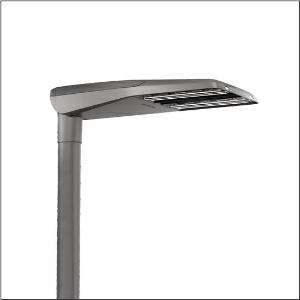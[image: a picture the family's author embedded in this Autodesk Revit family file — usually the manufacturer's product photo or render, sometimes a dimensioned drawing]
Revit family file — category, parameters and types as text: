
# Revit family: streetlight_sl_11_iq_midi___st1_2a_5xc3a51e08le_ac55
name_source: partatom
category: Lighting Fixtures
units: mm (PartAtom-declared; Revit-internal decimal feet)

## family parameters
Cut with Voids When Loaded = No
Host = Face
Light Source = No
Part Type = Normal
Room Calculation Point = No
Round Connector Dimension = Use Diameter
Shared = No

## types (1)
- --- (1 x LED, 9210 lm, 60.4 W, 3000K)
    Apparent Load = 60 VA
    CIE Flux Codes = 32 70 96 100 100
    Color Rendering = 70
    Color Temperature = 3000K
    Default Elevation = 1800 mm
    Description = Streetlight SL 11 iQ midi, mast luminaire, primary light control with 3 zone facetted reflector, of plastic, silver coated, highly specular, primary optical cover: cover, of PMMA, transparent, light distribution: ST1.2a, light emission: direct distribution, primary light characteristic: asymmetric, installation type: post-top, side-entry, LED, High Power LED, rated luminous flux: 9.210lm, luminous efficacy: 153lm/W, light colour: 730, colour temperature: 3000K, control: optimised constant luminous flux control (CLO 2.0), Desk-Remote (wireless, voltage-free reading and setting of iQ features in the workshop via application-optimized NFC function/RFID function), Light-Fading, Smart-Wire, Night-Set, Lumen-Switch, Temp-Guard, Auto-Match, with cable H07RN-F 5x 1.5mm², mains connection: 230..240V, AC, 50/60Hz, connection cable pre-assembled, cable length: 8,5m, start of lifetime: 60W, end of service life: 63W, reduction: 30W, luminaire housing, of diecast aluminium, powder-coated, Siteco® metallic grey (DB 702S), please order mast flange separately, inclination adjustable without tools: 0°, 5°, 10°, 15° (post-top) | 0°, -5°, -10°, -15° (side-entry), sealing non-destructively replaceable, multi-level sealing system, length: 780mm, width: 376mm, height: 118mm, mast flange for spigot size: 42mm (side-entry): 5XC10008XM4, 60/48mm (side-entry/post-top): 5XC10108XM2, 76/60mm (side-entry/post-top): 5XC10108XM1, equipment: standard, protection rating (complete): IP66, insulation class (complete): insulation class II (safety insulation), certification: CE, ENEC, VDE, impact resistance: IK09, permissible operating ambient temperature for outdoor applications: -25..+50°C, standard-compliant lighting for roads and squares, Environmental Product Declaration (EPD) tested and certified by an independent institute, packaging unit: 1 piece

Light Distribution: ST1.2a
    Height = 118 mm
    Lamp = 1 x LED
    Lamp Light Flux = 9210 lm
    Lamp Power = 60.4 W
    Lamp count = 1
    Length = 780 mm
    Luminous efficacy = 152 lm/W
    Manufacturer = Siteco
    ModVariant = No
    Model = 5XC3A51E08LE
    Number of Poles = 1
    OnlyDefault = Yes
    Power Factor = 1
    Product Name = Streetlight SL 11 iQ midi | ST1.2a
    Product group = mast luminaire | pylon top
    ProductGroupID = 6100
    Protection Class = Protection class II
    Protection Degree = IP 66
    RLX_Detail_Level = 1
    RLX_Emergency_Light_Flux = 0 lm
    RLX_Emergency_Type = 0
    RLX_Emergency_Type_DB = No
    RlxData = <blob elided: 70617 chars, md5=67c6e87c>
    Socket = socket
    Standby Power = 0 W
    System Light Flux = 9210 lm
    System Power = 60 W
    Type Comments = factory setting: luminous flux: 100 % | dim-lin: 254 | 520 mA
    Type Image = l_1005960.jpg
    URL = http://relux.com
    VarID = @adj_132751
    Voltage = 0 V
    Weight = 0.00 kg
    Width = 376 mm

## geometry (parser evidence)
native form markers: Blend x4, Sweep x8
no freeform markers — native parametric forms only
